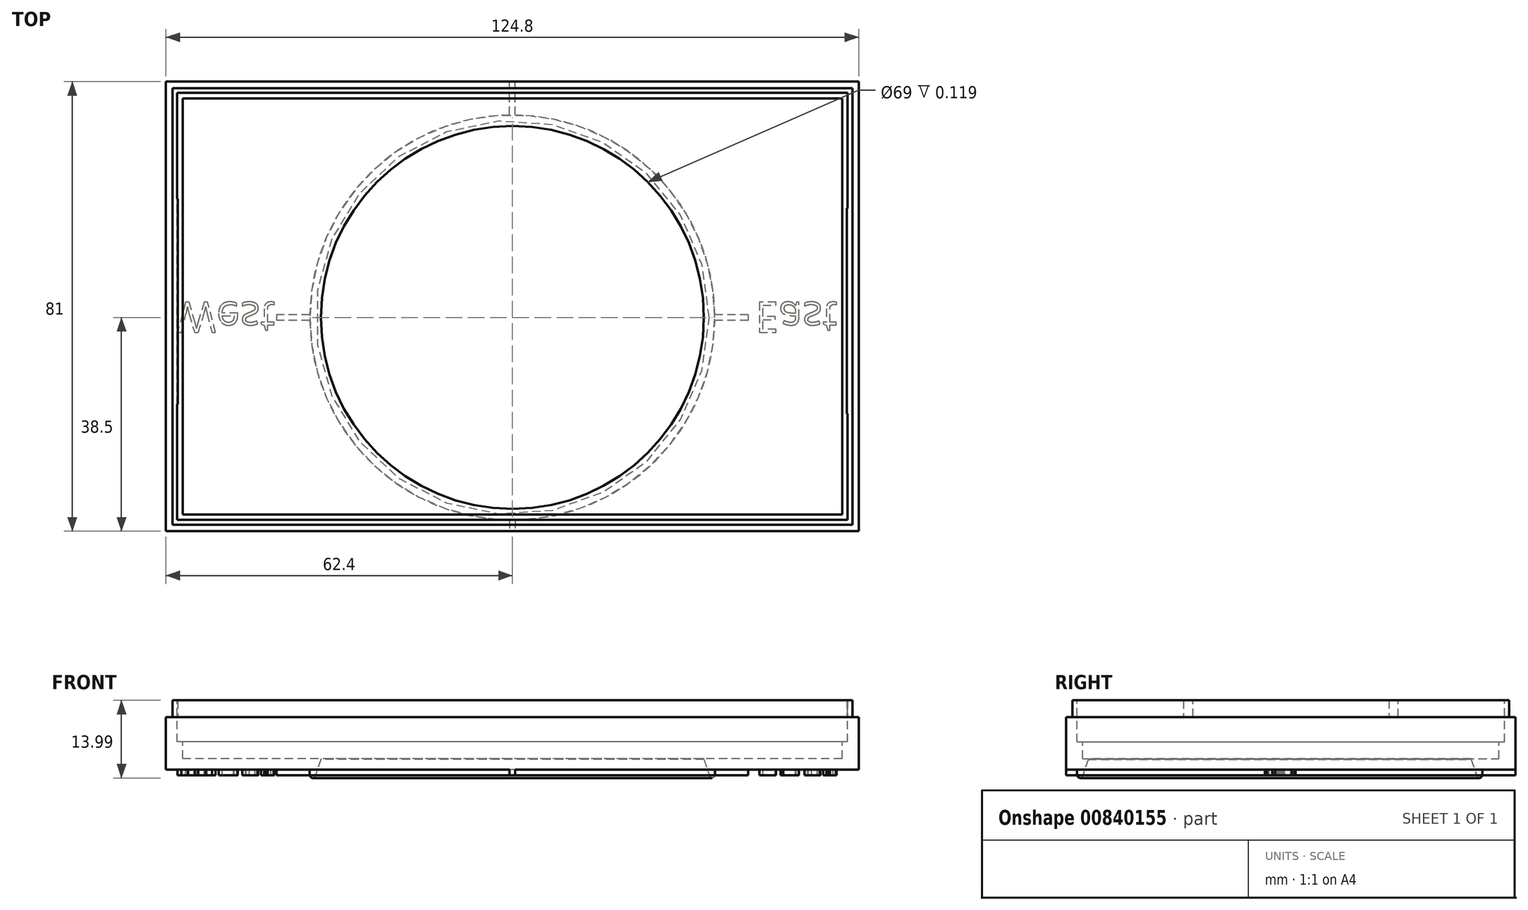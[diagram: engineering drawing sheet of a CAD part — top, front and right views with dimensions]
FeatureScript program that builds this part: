
annotation { "Feature Type Name" : "Feature", "Feature Type Description" : "" }
export const myFeature = defineFeature(function(context is Context, id is Id, definition is map)
    precondition{}
    {
        {
            var Q0;
            Q0=qCreatedBy(makeId("Top.planeOp"),FACE);
            var sketch = newSketch(context, id + "F0", { "sketchPlane" : qUnion([Q0])});
            skLineSegment(sketch, "E0.bottom", {"start": v(62.4, -40.5) * mm, "end": v(-62.4, -40.5) * mm});
            skLineSegment(sketch, "E0.top", {"start": v(62.4, 40.5) * mm, "end": v(-62.4, 40.5) * mm});
            skLineSegment(sketch, "E0.left", {"start": v(62.4, -40.5) * mm, "end": v(62.4, 40.5) * mm});
            skLineSegment(sketch, "E0.right", {"start": v(-62.4, -40.5) * mm, "end": v(-62.4, 40.5) * mm});
            skPoint(sketch, "E0.middle", {"position": v(0, 0) * mm});
            skSolve(sketch);
        }
        {
            var Q0;
            Q0=qSketchRegion(id+"F0",true);
            extrude(context, id + "F1", {"entities" : qUnion([Q0]), "depth" : 12.5 * mm, "offsetDistance" : 25 * mm});
        }
        {
            var Q0;
            Q0=makeQuery(id+"F1.opExtrude","CAP_FACE",FACE,{"disambiguationData":[OSD([sQuery(id+"F0.wireOp",EDGE,"E0.bottom"),sQuery(id+"F0.wireOp",EDGE,"E0.top"),sQuery(id+"F0.wireOp",EDGE,"E0.left"),sQuery(id+"F0.wireOp",EDGE,"E0.right")])],"isStart":false});
            var sketch = newSketch(context, id + "F2", { "sketchPlane" : qUnion([Q0])});
            skLineSegment(sketch, "E1.bottom", {"start": v(60.4, -38.5) * mm, "end": v(-60.4, -38.5) * mm});
            skLineSegment(sketch, "E1.top", {"start": v(60.4, 38.5) * mm, "end": v(-60.4, 38.5) * mm});
            skLineSegment(sketch, "E1.left", {"start": v(60.4, -38.5) * mm, "end": v(60.4, 38.5) * mm});
            skLineSegment(sketch, "E1.right", {"start": v(-60.4, -38.5) * mm, "end": v(-60.4, 38.5) * mm});
            skPoint(sketch, "E1.middle", {"position": v(0, 0) * mm});
            skSolve(sketch);
        }
        {
            var Q0;
            Q0=makeQuery(id+"F2.imprint","IMPRINT",FACE,{"disambiguationData":[TD([[makeQuery(id+"F2.imprint","IMPRINT",EDGE,{"derivedFrom":sQuery(id+"F2.wireOp",EDGE,"E1.bottom")}),-1.0]])]});
            extrude(context, id + "F3", {"entities" : qUnion([Q0]), "operationType" : NewBodyOperationType.REMOVE, "oppositeDirection" : true, "depth" : 7.5 * mm, "offsetDistance" : 25 * mm});
        }
        {
            var Q0;
            Q0=makeQuery(id+"F1.opExtrude","CAP_FACE",FACE,{"disambiguationData":[OSD([sQuery(id+"F0.wireOp",EDGE,"E0.bottom"),sQuery(id+"F0.wireOp",EDGE,"E0.top"),sQuery(id+"F0.wireOp",EDGE,"E0.left"),sQuery(id+"F0.wireOp",EDGE,"E0.right")])],"isStart":true});
            var sketch = newSketch(context, id + "F4", { "sketchPlane" : qUnion([Q0])});
            skCircle(sketch, "E2", {"center": v(0, 2) * mm, "radius": 36.5 * mm});
            skSolve(sketch);
        }
        {
            var Q0;
            Q0=makeQuery(id+"F4.imprint","IMPRINT",FACE,{"disambiguationData":[TD([[makeQuery(id+"F4.imprint","IMPRINT",EDGE,{"derivedFrom":sQuery(id+"F4.wireOp",EDGE,"E2")}),1.0]])]});
            extrude(context, id + "F5", {"entities" : qUnion([Q0]), "operationType" : NewBodyOperationType.ADD, "depth" : 1 * mm});
        }
        {
            var Q0;
            Q0=makeQuery(id+"F5.opExtrude","CAP_FACE",FACE,{"disambiguationData":[OSD([sQuery(id+"F4.wireOp",EDGE,"E2")])],"isStart":false});
            var sketch = newSketch(context, id + "F6", { "sketchPlane" : qUnion([Q0])});
            skCircle(sketch, "E3", {"center": v(0, 2) * mm, "radius": 34.5 * mm});
            skSolve(sketch);
        }
        {
            var Q0;
            Q0=makeQuery(id+"F6.imprint","IMPRINT",FACE,{"disambiguationData":[TD([[makeQuery(id+"F6.imprint","IMPRINT",EDGE,{"derivedFrom":sQuery(id+"F6.wireOp",EDGE,"E3")}),1.0]])]});
            extrude(context, id + "F7", {"entities" : qUnion([Q0]), "operationType" : NewBodyOperationType.REMOVE, "endBound" : BoundingType.THROUGH_ALL, "oppositeDirection" : true, "depth" : 25 * mm});
        }
        {
            var Q0;
            Q0=qCreatedBy(makeId("Top.planeOp"),FACE);
            var sketch = newSketch(context, id + "F8", { "sketchPlane" : qUnion([Q0])});
            skCircle(sketch, "E4", {"center": v(0, -2) * mm, "radius": 35.5 * mm});
            skSolve(sketch);
        }
        {
            var Q0;
            Q0=qCreatedBy(makeId("Front.planeOp"),FACE);
            var sketch = newSketch(context, id + "F9", { "sketchPlane" : qUnion([Q0])});
            skLineSegment(sketch, "E5", {"start": v(34.42, -1.03) * mm, "end": v(35.42, -1.03) * mm});
            skLineSegment(sketch, "E6", {"start": v(35.42, -1.03) * mm, "end": v(34.39, 2.05) * mm});
            skLineSegment(sketch, "E7", {"start": v(34.39, 2.05) * mm, "end": v(34.42, -1.03) * mm});
            skSolve(sketch);
        }
        {
            var Q0;
            Q0=qSketchRegion(id+"F9",true);
            var Q1;
            Q1=qConstructionFilter(qBodyType(qCreatedBy(id+"F8",EDGE),BodyType.WIRE),ConstructionObject.NO);
            sweep(context, id + "F10", {"operationType" : NewBodyOperationType.REMOVE, "profiles" : qUnion([Q0]), "path" : qUnion([Q1])});
        }
        {
            var Q0;
            Q0=qCreatedBy(makeId("Top.planeOp"),FACE);
            cPlane(context, id + "F11", {"entities" : qUnion([Q0]), "cplaneType" : CPlaneType.OFFSET, "offset" : 1 * mm, "oppositeDirection" : true, "width" : 150 * mm, "height" : 150 * mm});
        }
        {
            var Q0;
            Q0=qCreatedBy(id+"F11.planeOp",FACE);
            var sketch = newSketch(context, id + "F12", { "sketchPlane" : qUnion([Q0])});
            skCircle(sketch, "E8", {"center": v(0, -2) * mm, "radius": 36 * mm});
            skSolve(sketch);
        }
        {
            var Q0;
            Q0=qCreatedBy(makeId("Front.planeOp"),FACE);
            var sketch = newSketch(context, id + "F13", { "sketchPlane" : qUnion([Q0])});
            skCircle(sketch, "E9", {"center": v(35.91, -1) * mm, "radius": 0.5 * mm});
            skSolve(sketch);
        }
        {
            var Q0;
            Q0=makeQuery(id+"F13.imprint","IMPRINT",FACE,{"disambiguationData":[TD([[makeQuery(id+"F13.imprint","IMPRINT",EDGE,{"derivedFrom":sQuery(id+"F13.wireOp",EDGE,"E9")}),1.0]])]});
            var Q1;
            Q1=sQuery(id+"F12.wireOp",EDGE,"E8");
            revolve(context, id + "F14", {"operationType" : NewBodyOperationType.ADD, "entities" : qUnion([Q0]), "axis" : qUnion([Q1]), "revolveType" : RevolveType.FULL});
        }
        {
            var Q0;
            Q0=makeQuery(id+"F1.opExtrude","CAP_FACE",FACE,{"disambiguationData":[OSD([sQuery(id+"F0.wireOp",EDGE,"E0.bottom"),sQuery(id+"F0.wireOp",EDGE,"E0.top"),sQuery(id+"F0.wireOp",EDGE,"E0.left"),sQuery(id+"F0.wireOp",EDGE,"E0.right")])],"isStart":true});
            var sketch = newSketch(context, id + "F15", { "sketchPlane" : qUnion([Q0])});
            skLineSegment(sketch, "E10.bottom", {"start": v(-36.5, 1.5) * mm, "end": v(-42.5, 1.5) * mm});
            skLineSegment(sketch, "E10.top", {"start": v(-36.5, 2.5) * mm, "end": v(-42.5, 2.5) * mm});
            skLineSegment(sketch, "E10.left", {"start": v(-36.5, 1.5) * mm, "end": v(-36.5, 2.5) * mm});
            skLineSegment(sketch, "E10.right", {"start": v(-42.5, 1.5) * mm, "end": v(-42.5, 2.5) * mm});
            skPoint(sketch, "E10.middle", {"position": v(-39.5, 2) * mm});
            skSolve(sketch);
        }
        {
            var Q0;
            Q0=qSketchRegion(id+"F15",true);
            extrude(context, id + "F16", {"entities" : qUnion([Q0]), "operationType" : NewBodyOperationType.ADD, "depth" : 1 * mm});
        }
        {
            var Q0;
            Q0=makeQuery(id+"F1.opExtrude","CAP_FACE",FACE,{"disambiguationData":[OSD([sQuery(id+"F0.wireOp",EDGE,"E0.bottom"),sQuery(id+"F0.wireOp",EDGE,"E0.top"),sQuery(id+"F0.wireOp",EDGE,"E0.left"),sQuery(id+"F0.wireOp",EDGE,"E0.right")])],"isStart":true});
            var sketch = newSketch(context, id + "F17", { "sketchPlane" : qUnion([Q0])});
            skLineSegment(sketch, "E11.bottom", {"start": v(42.5, 1.5) * mm, "end": v(36.5, 1.5) * mm});
            skLineSegment(sketch, "E11.top", {"start": v(42.5, 2.5) * mm, "end": v(36.5, 2.5) * mm});
            skLineSegment(sketch, "E11.left", {"start": v(42.5, 1.5) * mm, "end": v(42.5, 2.5) * mm});
            skLineSegment(sketch, "E11.right", {"start": v(36.5, 1.5) * mm, "end": v(36.5, 2.5) * mm});
            skPoint(sketch, "E11.middle", {"position": v(39.5, 2) * mm});
            skSolve(sketch);
        }
        {
            var Q0;
            Q0=qSketchRegion(id+"F17",true);
            extrude(context, id + "F18", {"entities" : qUnion([Q0]), "operationType" : NewBodyOperationType.ADD, "depth" : 1 * mm});
        }
        {
            var Q0;
            Q0=makeQuery(id+"F1.opExtrude","CAP_FACE",FACE,{"disambiguationData":[OSD([sQuery(id+"F0.wireOp",EDGE,"E0.bottom"),sQuery(id+"F0.wireOp",EDGE,"E0.top"),sQuery(id+"F0.wireOp",EDGE,"E0.left"),sQuery(id+"F0.wireOp",EDGE,"E0.right")])],"isStart":true});
            var sketch = newSketch(context, id + "F19", { "sketchPlane" : qUnion([Q0])});
            skLineSegment(sketch, "E12.bottom", {"start": v(0.5, -34.47) * mm, "end": v(-0.5, -34.47) * mm});
            skLineSegment(sketch, "E12.top", {"start": v(0.5, -40.47) * mm, "end": v(-0.5, -40.47) * mm});
            skLineSegment(sketch, "E12.left", {"start": v(0.5, -34.47) * mm, "end": v(0.5, -40.47) * mm});
            skLineSegment(sketch, "E12.right", {"start": v(-0.5, -34.47) * mm, "end": v(-0.5, -40.47) * mm});
            skPoint(sketch, "E12.middle", {"position": v(0, -37.47) * mm});
            skSolve(sketch);
        }
        {
            var Q0;
            Q0=qSketchRegion(id+"F19",true);
            extrude(context, id + "F20", {"entities" : qUnion([Q0]), "operationType" : NewBodyOperationType.ADD, "depth" : 1 * mm});
        }
        {
            var Q0;
            Q0=makeQuery(id+"F1.opExtrude","CAP_FACE",FACE,{"disambiguationData":[OSD([sQuery(id+"F0.wireOp",EDGE,"E0.bottom"),sQuery(id+"F0.wireOp",EDGE,"E0.top"),sQuery(id+"F0.wireOp",EDGE,"E0.left"),sQuery(id+"F0.wireOp",EDGE,"E0.right")])],"isStart":true});
            var sketch = newSketch(context, id + "F21", { "sketchPlane" : qUnion([Q0])});
            skLineSegment(sketch, "E13.bottom", {"start": v(0.5, 38.5) * mm, "end": v(-0.5, 38.5) * mm});
            skLineSegment(sketch, "E13.top", {"start": v(0.5, 40.5) * mm, "end": v(-0.5, 40.5) * mm});
            skLineSegment(sketch, "E13.left", {"start": v(0.5, 38.5) * mm, "end": v(0.5, 40.5) * mm});
            skLineSegment(sketch, "E13.right", {"start": v(-0.5, 38.5) * mm, "end": v(-0.5, 40.5) * mm});
            skPoint(sketch, "E13.middle", {"position": v(0, 39.5) * mm});
            skSolve(sketch);
        }
        {
            var Q0;
            Q0=qSketchRegion(id+"F21",true);
            extrude(context, id + "F22", {"entities" : qUnion([Q0]), "operationType" : NewBodyOperationType.ADD, "depth" : 1 * mm});
        }
        {
            var Q0;
            Q0=makeQuery(id+"F1.opExtrude","CAP_FACE",FACE,{"disambiguationData":[OSD([sQuery(id+"F0.wireOp",EDGE,"E0.bottom"),sQuery(id+"F0.wireOp",EDGE,"E0.top"),sQuery(id+"F0.wireOp",EDGE,"E0.left"),sQuery(id+"F0.wireOp",EDGE,"E0.right")])],"isStart":true});
            var sketch = newSketch(context, id + "F23", { "sketchPlane" : qUnion([Q0])});
            skText(sketch, "E14", { "text": " West", "fontName": "OpenSans-Regular.ttf"});
            const initialGuessF23  = {"E14": [-0.0624, -0.00075, 1, 0, 0.0055]};
            skSetInitialGuess(sketch, initialGuessF23);
            skSolve(sketch);
        }
        {
            var Q0;
            Q0=qSketchRegion(id+"F23",true);
            extrude(context, id + "F24", {"entities" : qUnion([Q0]), "operationType" : NewBodyOperationType.ADD, "depth" : 1 * mm});
        }
        {
            var Q0;
            {var subQ0=sQuery(id+"F0.wireOp",EDGE,"E0.right");var subQ1=sQuery(id+"F0.wireOp",EDGE,"E0.left");var subQ2=sQuery(id+"F0.wireOp",EDGE,"E0.bottom");var subQ3=sQuery(id+"F0.wireOp",EDGE,"E0.top");Q0=makeQuery(id+"F24.boolean.opBoolean","SPLIT",FACE,{"disambiguationData":[TD([makeQuery(id+"F1.opExtrude","SWEPT_FACE",FACE,{"disambiguationData":[OSD([subQ2])]})])],"derivedFrom":makeQuery(id+"F1.opExtrude","CAP_FACE",FACE,{"disambiguationData":[OSD([subQ2,subQ3,subQ1,subQ0])],"isStart":true})});}
            var sketch = newSketch(context, id + "F25", { "sketchPlane" : qUnion([Q0])});
            skText(sketch, "E15", { "text": "East", "fontName": "OpenSans-Regular.ttf"});
            const initialGuessF25  = {"E15": [0.04373, -0.00075, 1, 0, 0.0055]};
            skSetInitialGuess(sketch, initialGuessF25);
            skSolve(sketch);
        }
        {
            var Q0;
            Q0=qSketchRegion(id+"F25",true);
            extrude(context, id + "F26", {"entities" : qUnion([Q0]), "operationType" : NewBodyOperationType.ADD, "depth" : 1 * mm});
        }
        {
            var Q0;
            Q0=makeQuery(id+"F1.opExtrude","CAP_FACE",FACE,{"disambiguationData":[OSD([sQuery(id+"F0.wireOp",EDGE,"E0.bottom"),sQuery(id+"F0.wireOp",EDGE,"E0.top"),sQuery(id+"F0.wireOp",EDGE,"E0.left"),sQuery(id+"F0.wireOp",EDGE,"E0.right")])],"isStart":false});
            var sketch = newSketch(context, id + "F27", { "sketchPlane" : qUnion([Q0])});
            skLineSegment(sketch, "E16.bottom", {"start": v(-62.4, -40.5) * mm, "end": v(-61.25, -40.5) * mm});
            skLineSegment(sketch, "E16.top", {"start": v(-62.4, 40.5) * mm, "end": v(-61.25, 40.5) * mm});
            skLineSegment(sketch, "E16.left", {"start": v(-62.4, -40.5) * mm, "end": v(-62.4, 40.5) * mm});
            skLineSegment(sketch, "E16.right", {"start": v(-61.25, -40.5) * mm, "end": v(-61.25, 40.5) * mm});
            skSolve(sketch);
        }
        {
            var Q0;
            Q0=qSketchRegion(id+"F27",true);
            extrude(context, id + "F28", {"entities" : qUnion([Q0]), "operationType" : NewBodyOperationType.REMOVE, "oppositeDirection" : true, "depth" : 3 * mm, "offsetDistance" : 25 * mm});
        }
        {
            var Q0;
            Q0=makeQuery(id+"F1.opExtrude","CAP_FACE",FACE,{"disambiguationData":[OSD([sQuery(id+"F0.wireOp",EDGE,"E0.bottom"),sQuery(id+"F0.wireOp",EDGE,"E0.top"),sQuery(id+"F0.wireOp",EDGE,"E0.left"),sQuery(id+"F0.wireOp",EDGE,"E0.right")])],"isStart":false});
            var sketch = newSketch(context, id + "F29", { "sketchPlane" : qUnion([Q0])});
            skLineSegment(sketch, "E17.bottom", {"start": v(62.4, -40.5) * mm, "end": v(61.25, -40.5) * mm});
            skLineSegment(sketch, "E17.top", {"start": v(62.4, 40.5) * mm, "end": v(61.25, 40.5) * mm});
            skLineSegment(sketch, "E17.left", {"start": v(62.4, -40.5) * mm, "end": v(62.4, 40.5) * mm});
            skLineSegment(sketch, "E17.right", {"start": v(61.25, -40.5) * mm, "end": v(61.25, 40.5) * mm});
            skSolve(sketch);
        }
        {
            var Q0;
            Q0=qSketchRegion(id+"F29",true);
            extrude(context, id + "F30", {"entities" : qUnion([Q0]), "operationType" : NewBodyOperationType.REMOVE, "oppositeDirection" : true, "depth" : 3 * mm, "offsetDistance" : 25 * mm});
        }
        {
            var Q0;
            Q0=makeQuery(id+"F1.opExtrude","CAP_FACE",FACE,{"disambiguationData":[OSD([sQuery(id+"F0.wireOp",EDGE,"E0.bottom"),sQuery(id+"F0.wireOp",EDGE,"E0.top"),sQuery(id+"F0.wireOp",EDGE,"E0.left"),sQuery(id+"F0.wireOp",EDGE,"E0.right")])],"isStart":false});
            var sketch = newSketch(context, id + "F31", { "sketchPlane" : qUnion([Q0])});
            skLineSegment(sketch, "E18.bottom", {"start": v(-61.25, 40.5) * mm, "end": v(61.25, 40.5) * mm});
            skLineSegment(sketch, "E18.top", {"start": v(-61.25, 39.35) * mm, "end": v(61.25, 39.35) * mm});
            skLineSegment(sketch, "E18.left", {"start": v(-61.25, 40.5) * mm, "end": v(-61.25, 39.35) * mm});
            skLineSegment(sketch, "E18.right", {"start": v(61.25, 40.5) * mm, "end": v(61.25, 39.35) * mm});
            skSolve(sketch);
        }
        {
            var Q0;
            Q0=makeQuery(id+"F31.imprint","IMPRINT",FACE,{"disambiguationData":[TD([[makeQuery(id+"F31.imprint","IMPRINT",EDGE,{"derivedFrom":sQuery(id+"F31.wireOp",EDGE,"E18.bottom")}),1.0]])]});
            extrude(context, id + "F32", {"entities" : qUnion([Q0]), "operationType" : NewBodyOperationType.REMOVE, "oppositeDirection" : true, "depth" : 3 * mm, "offsetDistance" : 25 * mm});
        }
        {
            var Q0;
            Q0=makeQuery(id+"F1.opExtrude","CAP_FACE",FACE,{"disambiguationData":[OSD([sQuery(id+"F0.wireOp",EDGE,"E0.bottom"),sQuery(id+"F0.wireOp",EDGE,"E0.top"),sQuery(id+"F0.wireOp",EDGE,"E0.left"),sQuery(id+"F0.wireOp",EDGE,"E0.right")])],"isStart":false});
            var sketch = newSketch(context, id + "F33", { "sketchPlane" : qUnion([Q0])});
            skLineSegment(sketch, "E19.bottom", {"start": v(-61.25, -40.5) * mm, "end": v(61.25, -40.5) * mm});
            skLineSegment(sketch, "E19.top", {"start": v(-61.25, -39.35) * mm, "end": v(61.25, -39.35) * mm});
            skLineSegment(sketch, "E19.left", {"start": v(-61.25, -40.5) * mm, "end": v(-61.25, -39.35) * mm});
            skLineSegment(sketch, "E19.right", {"start": v(61.25, -40.5) * mm, "end": v(61.25, -39.35) * mm});
            skSolve(sketch);
        }
        {
            var Q0;
            Q0=qSketchRegion(id+"F33",true);
            extrude(context, id + "F34", {"entities" : qUnion([Q0]), "operationType" : NewBodyOperationType.REMOVE, "oppositeDirection" : true, "depth" : 3 * mm, "offsetDistance" : 25 * mm});
        }
        {
            var Q0;
            Q0=makeQuery(id+"F30.boolean.opBoolean","COPY",FACE,{"derivedFrom":makeQuery(id+"F30.opExtrude","SWEPT_FACE",FACE,{"disambiguationData":[OSD([sQuery(id+"F29.wireOp",EDGE,"E17.right")])]})});
            var sketch = newSketch(context, id + "F35", { "sketchPlane" : qUnion([Q0])});
            skLineSegment(sketch, "E20.bottom", {"start": v(-19.35, 12.5) * mm, "end": v(17.65, 12.5) * mm});
            skLineSegment(sketch, "E20.top", {"start": v(-19.35, 9.5) * mm, "end": v(17.65, 9.5) * mm});
            skLineSegment(sketch, "E20.left", {"start": v(-19.35, 12.5) * mm, "end": v(-19.35, 9.5) * mm});
            skLineSegment(sketch, "E20.right", {"start": v(17.65, 12.5) * mm, "end": v(17.65, 9.5) * mm});
            skSolve(sketch);
        }
        {
            var Q0;
            Q0=qSketchRegion(id+"F35",true);
            extrude(context, id + "F36", {"entities" : qUnion([Q0]), "operationType" : NewBodyOperationType.ADD, "oppositeDirection" : true, "depth" : 1 * mm, "offsetDistance" : 25 * mm});
        }
        {
            var Q0;
            Q0=makeQuery(id+"F28.boolean.opBoolean","COPY",FACE,{"derivedFrom":makeQuery(id+"F28.opExtrude","SWEPT_FACE",FACE,{"disambiguationData":[OSD([sQuery(id+"F27.wireOp",EDGE,"E16.right")])]})});
            var sketch = newSketch(context, id + "F37", { "sketchPlane" : qUnion([Q0])});
            skLineSegment(sketch, "E21.bottom", {"start": v(-19.35, 12.5) * mm, "end": v(17.65, 12.5) * mm});
            skLineSegment(sketch, "E21.top", {"start": v(-19.35, 9.5) * mm, "end": v(17.65, 9.5) * mm});
            skLineSegment(sketch, "E21.left", {"start": v(-19.35, 12.5) * mm, "end": v(-19.35, 9.5) * mm});
            skLineSegment(sketch, "E21.right", {"start": v(17.65, 12.5) * mm, "end": v(17.65, 9.5) * mm});
            skSolve(sketch);
        }
        {
            var Q0;
            Q0=qSketchRegion(id+"F37",true);
            extrude(context, id + "F38", {"entities" : qUnion([Q0]), "operationType" : NewBodyOperationType.ADD, "oppositeDirection" : true, "depth" : 1 * mm, "offsetDistance" : 25 * mm});
        }
        {
            var Q0;
            Q0=makeQuery(id+"F3.boolean.opBoolean","COPY",FACE,{"derivedFrom":makeQuery(id+"F3.opExtrude","CAP_FACE",FACE,{"disambiguationData":[OSD([sQuery(id+"F2.wireOp",EDGE,"E1.bottom"),sQuery(id+"F2.wireOp",EDGE,"E1.top"),sQuery(id+"F2.wireOp",EDGE,"E1.left"),sQuery(id+"F2.wireOp",EDGE,"E1.right")])],"isStart":false})});
            var sketch = newSketch(context, id + "F39", { "sketchPlane" : qUnion([Q0])});
            skLineSegment(sketch, "E22.bottom", {"start": v(59.4, -37.5) * mm, "end": v(-59.4, -37.5) * mm});
            skLineSegment(sketch, "E22.top", {"start": v(59.4, 37.5) * mm, "end": v(-59.4, 37.5) * mm});
            skLineSegment(sketch, "E22.left", {"start": v(59.4, -37.5) * mm, "end": v(59.4, 37.5) * mm});
            skLineSegment(sketch, "E22.right", {"start": v(-59.4, -37.5) * mm, "end": v(-59.4, 37.5) * mm});
            skPoint(sketch, "E22.middle", {"position": v(0, 0) * mm});
            skSolve(sketch);
        }
        {
            var Q0;
            Q0 = qSketchRegion(id + "F39", true);
            extrude(context, id + "F40", {"entities" : qUnion([Q0]), "operationType" : NewBodyOperationType.REMOVE, "oppositeDirection" : true, "depth" : 3 * mm, "offsetDistance" : 25 * mm});
        }
    });
